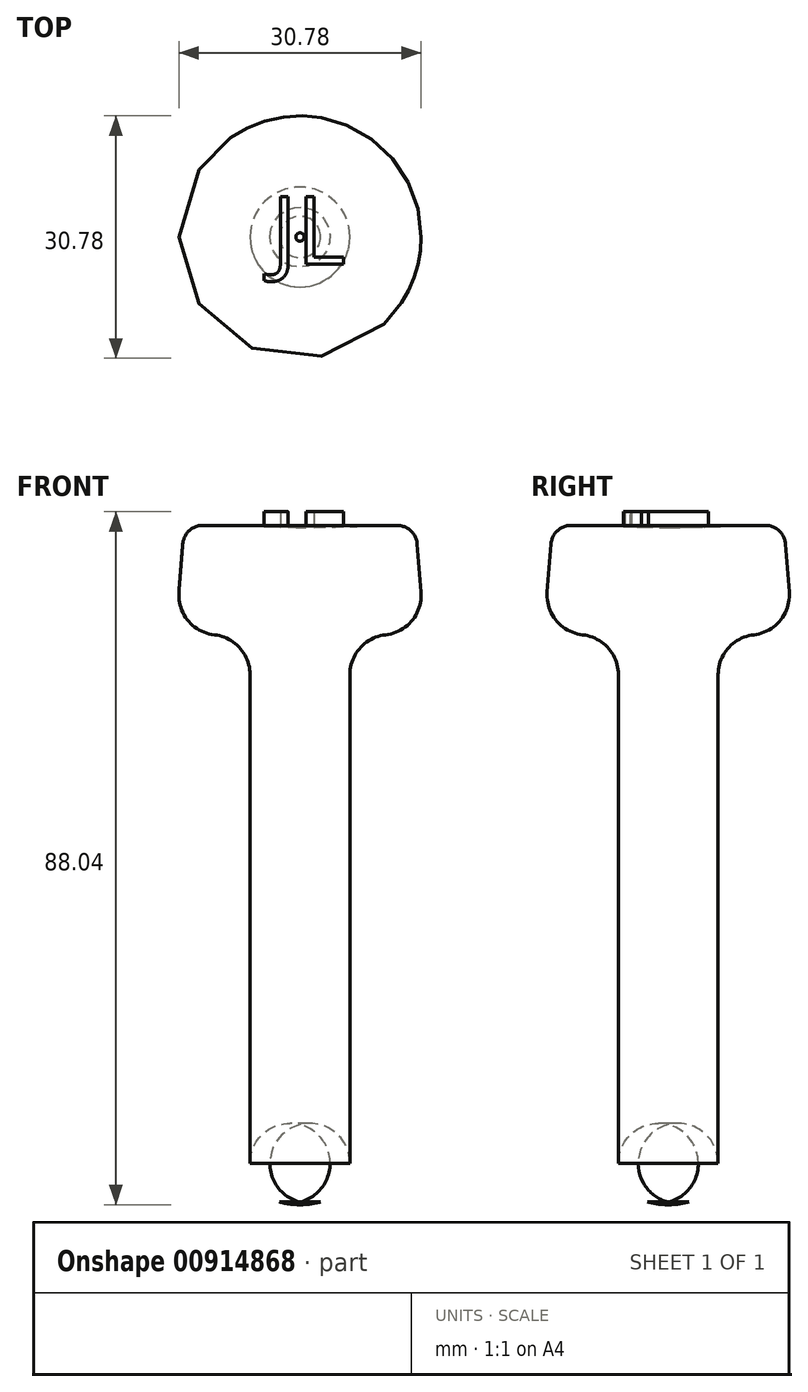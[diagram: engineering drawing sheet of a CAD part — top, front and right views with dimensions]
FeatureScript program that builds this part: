
annotation { "Feature Type Name" : "Feature", "Feature Type Description" : "" }
export const myFeature = defineFeature(function(context is Context, id is Id, definition is map)
    precondition{}
    {
        {
            var Q0;
            Q0=qCreatedBy(makeId("Front.planeOp"),FACE);
            var sketch = newSketch(context, id + "F0", { "sketchPlane" : qUnion([Q0])});
            skLineSegment(sketch, "E0.MirrorCS", {"start": v(6.34, -33.01) * mm, "end": v(6.34, 37.02) * mm});
            skArc(sketch, "E1", {"start": v(0, -35.34) * mm, "mid": v(3.38, -34.74) * mm, "end": v(6.34, -33.01) * mm});
            skLineSegment(sketch, "E2", {"start": v(0, -25.55) * mm, "end": v(0, 65.7) * mm});
            skLineSegment(sketch, "E3", {"start": v(0, 65.7) * mm, "end": v(0, -35.34) * mm});
            skPoint(sketch, "E4.end.orphan", {"position": v(-6.34, 37.75) * mm});
            skPoint(sketch, "E5.orphan", {"position": v(-6.34, -33.01) * mm});
            skLineSegment(sketch, "E6", {"start": v(0.53, 50.67) * mm, "end": v(14.7, 51) * mm});
            skLineSegment(sketch, "E7", {"start": v(0.53, 50.67) * mm, "end": v(0, 50.67) * mm});
            skLineSegment(sketch, "E8", {"start": v(6.34, 37.02) * mm, "end": v(15.81, 37.02) * mm});
            skLineSegment(sketch, "E9", {"start": v(15.81, 37.02) * mm, "end": v(14.7, 51) * mm});
            skPoint(sketch, "E10.orphan", {"position": v(6.34, 37.75) * mm});
            skSolve(sketch);
        }
        {
            var Q0;
            Q0=makeQuery(id+"F0.imprint","IMPRINT",FACE,{"disambiguationData":[TD([[makeQuery(id+"F0.imprint","IMPRINT",EDGE,{"derivedFrom":sQuery(id+"F0.wireOp",EDGE,"E0.MirrorCS")}),1.0]])]});
            var Q1;
            Q1=sQuery(id+"F0.wireOp",EDGE,"E2");
            revolve(context, id + "F1", {"surfaceOperationType" : NewSurfaceOperationType.NEW, "entities" : qUnion([Q0]), "axis" : qUnion([Q1]), "revolveType" : RevolveType.FULL});
        }
        {
            var Q0;
            Q0=makeQuery(id+"F1.opRevolve","SWEPT_EDGE",EDGE,{"disambiguationData":[OSD([sQuery(id+"F0.wireOp",EDGE,"E8"),sQuery(id+"F0.wireOp",EDGE,"E9")])]});
            fillet(context, id + "F2", {"entities" : qUnion([Q0]), "radius" : 5.08 * mm, "tangentPropagation" : true, "allowEdgeOverflow" : false});
        }
        {
            var Q0;
            Q0=makeQuery(id+"F1.opRevolve","SWEPT_EDGE",EDGE,{"disambiguationData":[OSD([sQuery(id+"F0.wireOp",EDGE,"E0.MirrorCS"),sQuery(id+"F0.wireOp",EDGE,"E1")])]});
            fillet(context, id + "F3", {"entities" : qUnion([Q0]), "radius" : 5.08 * mm, "tangentPropagation" : true, "allowEdgeOverflow" : false});
        }
        {
            var Q0;
            Q0=makeQuery(id+"F1.opRevolve","SWEPT_EDGE",EDGE,{"disambiguationData":[OSD([sQuery(id+"F0.wireOp",EDGE,"E6"),sQuery(id+"F0.wireOp",EDGE,"E9")])]});
            fillet(context, id + "F4", {"entities" : qUnion([Q0]), "radius" : 2.54 * mm, "tangentPropagation" : true, "allowEdgeOverflow" : false});
        }
        {
            var Q0;
            Q0=makeQuery(id+"F1.opRevolve","SWEPT_EDGE",EDGE,{"disambiguationData":[OSD([sQuery(id+"F0.wireOp",EDGE,"E0.MirrorCS"),sQuery(id+"F0.wireOp",EDGE,"E8")])]});
            fillet(context, id + "F5", {"entities" : qUnion([Q0]), "radius" : 5.08 * mm, "tangentPropagation" : true, "allowEdgeOverflow" : false});
        }
        {
            var Q0;
            Q0=makeQuery(id+"F1.opRevolve","SWEPT_FACE",FACE,{"disambiguationData":[OSD([sQuery(id+"F0.wireOp",EDGE,"E7")])]});
            var sketch = newSketch(context, id + "F6", { "sketchPlane" : qUnion([Q0])});
            skText(sketch, "E11", { "text": "JL", "fontName": "OpenSans-Regular.ttf"});
            const initialGuessF6  = {"E11": [-0.0036, -0.00343, 1, 0, 0.00862]};
            skSetInitialGuess(sketch, initialGuessF6);
            skSolve(sketch);
        }
        {
            var Q0;
            Q0 = qSketchRegion(id + "F6", true);
            extrude(context, id + "F7", {"entities" : qUnion([Q0]), "operationType" : NewBodyOperationType.ADD, "depth" : 2.03 * mm, "offsetDistance" : 25.4 * mm});
        }
    });
